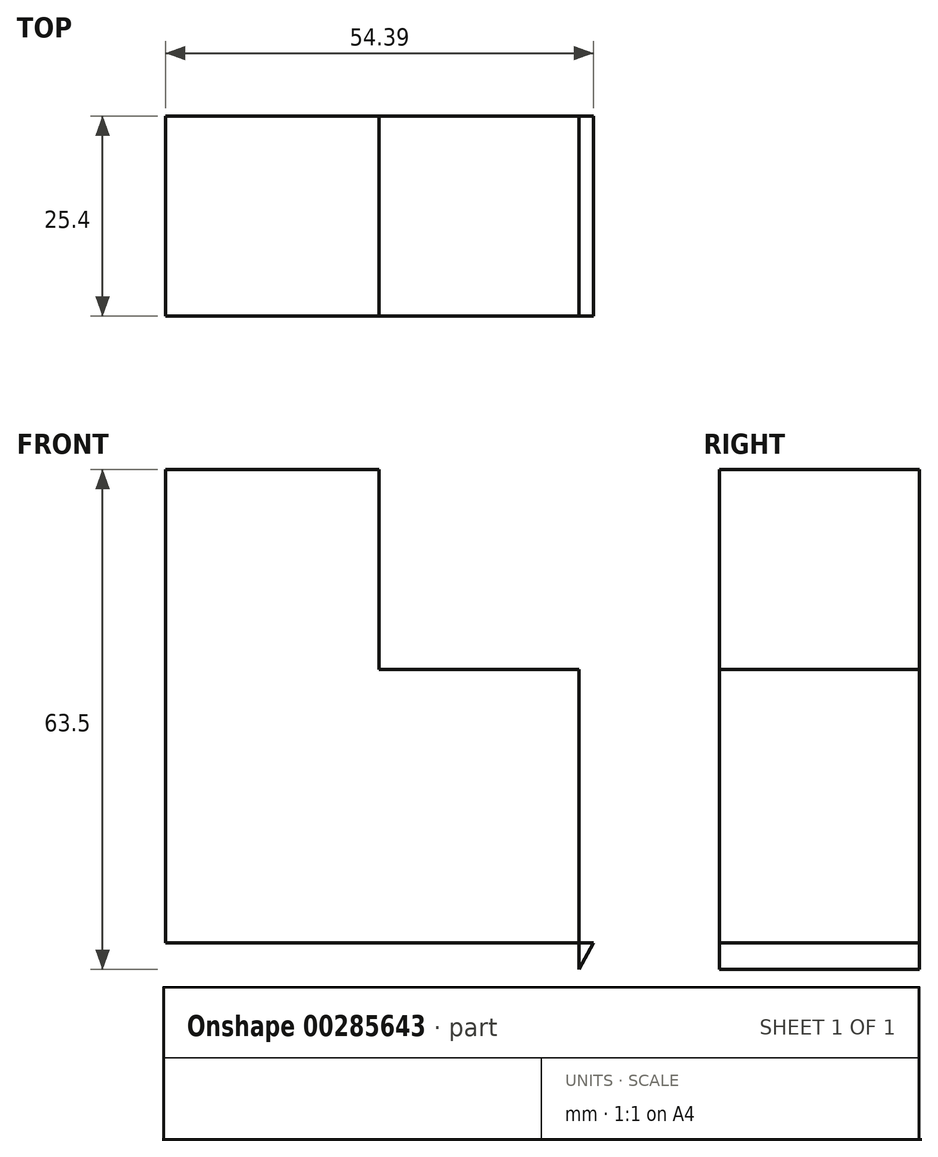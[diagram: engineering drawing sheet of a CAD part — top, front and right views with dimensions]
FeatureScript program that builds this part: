
annotation { "Feature Type Name" : "Feature", "Feature Type Description" : "" }
export const myFeature = defineFeature(function(context is Context, id is Id, definition is map)
    precondition{}
    {
        {
            var Q0;
            Q0=qCreatedBy(makeId("Front.planeOp"),FACE);
            var sketch = newSketch(context, id + "F0", { "sketchPlane" : qUnion([Q0])});
            skLineSegment(sketch, "E0", {"start": v(-58.42, 55.83) * mm, "end": v(-33.02, 55.83) * mm});
            skLineSegment(sketch, "E1", {"start": v(-33.02, 55.83) * mm, "end": v(-33.02, 30.43) * mm});
            skLineSegment(sketch, "E2", {"start": v(-33.02, 30.43) * mm, "end": v(-7.62, 30.43) * mm});
            skLineSegment(sketch, "E3", {"start": v(-7.62, 30.43) * mm, "end": v(-7.62, -7.67) * mm});
            skLineSegment(sketch, "E4", {"start": v(-7.62, -7.67) * mm, "end": v(-5.76, -4.32) * mm});
            skLineSegment(sketch, "E5", {"start": v(-5.76, -4.32) * mm, "end": v(-60.15, -4.32) * mm});
            skLineSegment(sketch, "E6", {"start": v(-60.15, -4.32) * mm, "end": v(-60.15, 55.83) * mm});
            skLineSegment(sketch, "E7", {"start": v(-60.15, 55.83) * mm, "end": v(-58.42, 55.83) * mm});
            skSolve(sketch);
        }
        {
            var Q0;
            Q0 = qSketchRegion(id + "F0", true);
            extrude(context, id + "F1", {"entities" : qUnion([Q0]), "depth" : 25.4 * mm});
        }
    });
